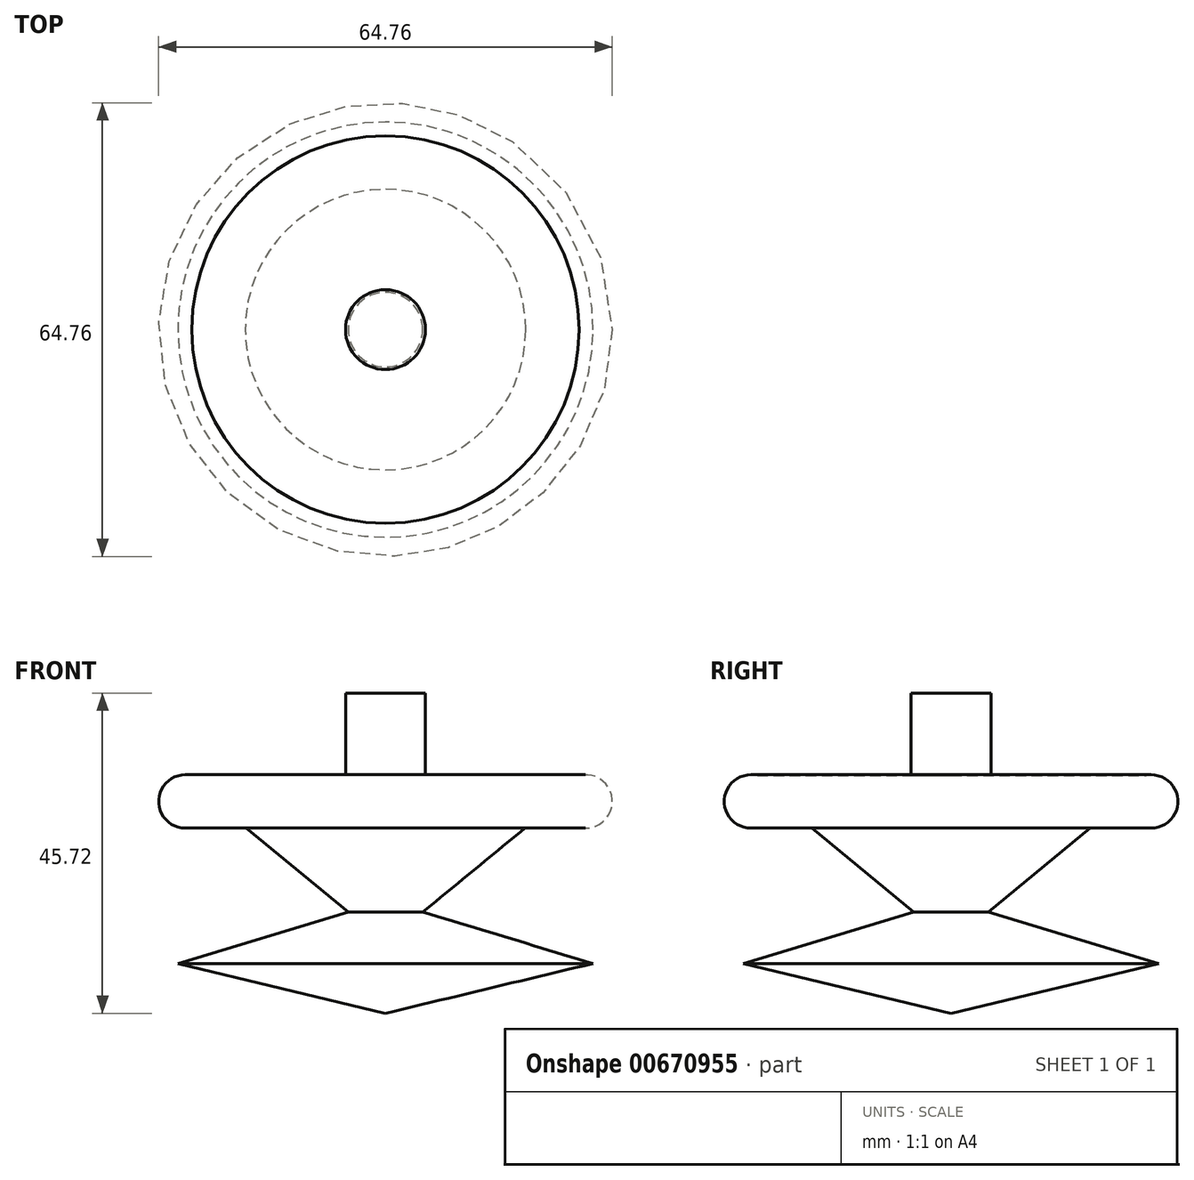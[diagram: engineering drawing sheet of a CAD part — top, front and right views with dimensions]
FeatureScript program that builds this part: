
annotation { "Feature Type Name" : "Feature", "Feature Type Description" : "" }
export const myFeature = defineFeature(function(context is Context, id is Id, definition is map)
    precondition{}
    {
        {
            var Q0;
            Q0=qCreatedBy(makeId("Front.planeOp"),FACE);
            var sketch = newSketch(context, id + "F0", { "sketchPlane" : qUnion([Q0])});
            skLineSegment(sketch, "E0", {"start": v(0, 0) * mm, "end": v(-29.64, 7.1) * mm});
            skLineSegment(sketch, "E1", {"start": v(-29.64, 7.1) * mm, "end": v(-5.32, 14.44) * mm});
            skArc(sketch, "E2", {"start": v(-27.65, 33.93) * mm, "mid": v(-32.38, 30.24) * mm, "end": v(-27.65, 26.54) * mm});
            skLineSegment(sketch, "E3", {"start": v(-27.65, 33.93) * mm, "end": v(-5.7, 33.93) * mm});
            skLineSegment(sketch, "E4", {"start": v(-5.7, 33.93) * mm, "end": v(-5.7, 45.72) * mm});
            skLineSegment(sketch, "E5", {"start": v(-5.7, 45.72) * mm, "end": v(0, 45.72) * mm});
            skLineSegment(sketch, "E6", {"start": v(0, 45.72) * mm, "end": v(0, 0) * mm});
            skLineSegment(sketch, "E7", {"start": v(-5.32, 14.44) * mm, "end": v(-20.03, 26.54) * mm});
            skLineSegment(sketch, "E8", {"start": v(-27.65, 26.54) * mm, "end": v(-20.03, 26.54) * mm});
            skSolve(sketch);
        }
        {
            var Q0;
            Q0 = qSketchRegion(id + "F0", true);
            var Q1;
            Q1=sQuery(id+"F0.wireOp",EDGE,"E6");
            revolve(context, id + "F1", {"entities" : qUnion([Q0]), "axis" : qUnion([Q1]), "revolveType" : RevolveType.FULL});
        }
        {
            var Q0;
            Q0 = qSketchRegion(id + "F0", true);
            var Q1;
            Q1=sQuery(id+"F0.wireOp",EDGE,"E6");
            revolve(context, id + "F2", {"entities" : qUnion([Q0]), "axis" : qUnion([Q1]), "revolveType" : RevolveType.FULL});
        }
    });
